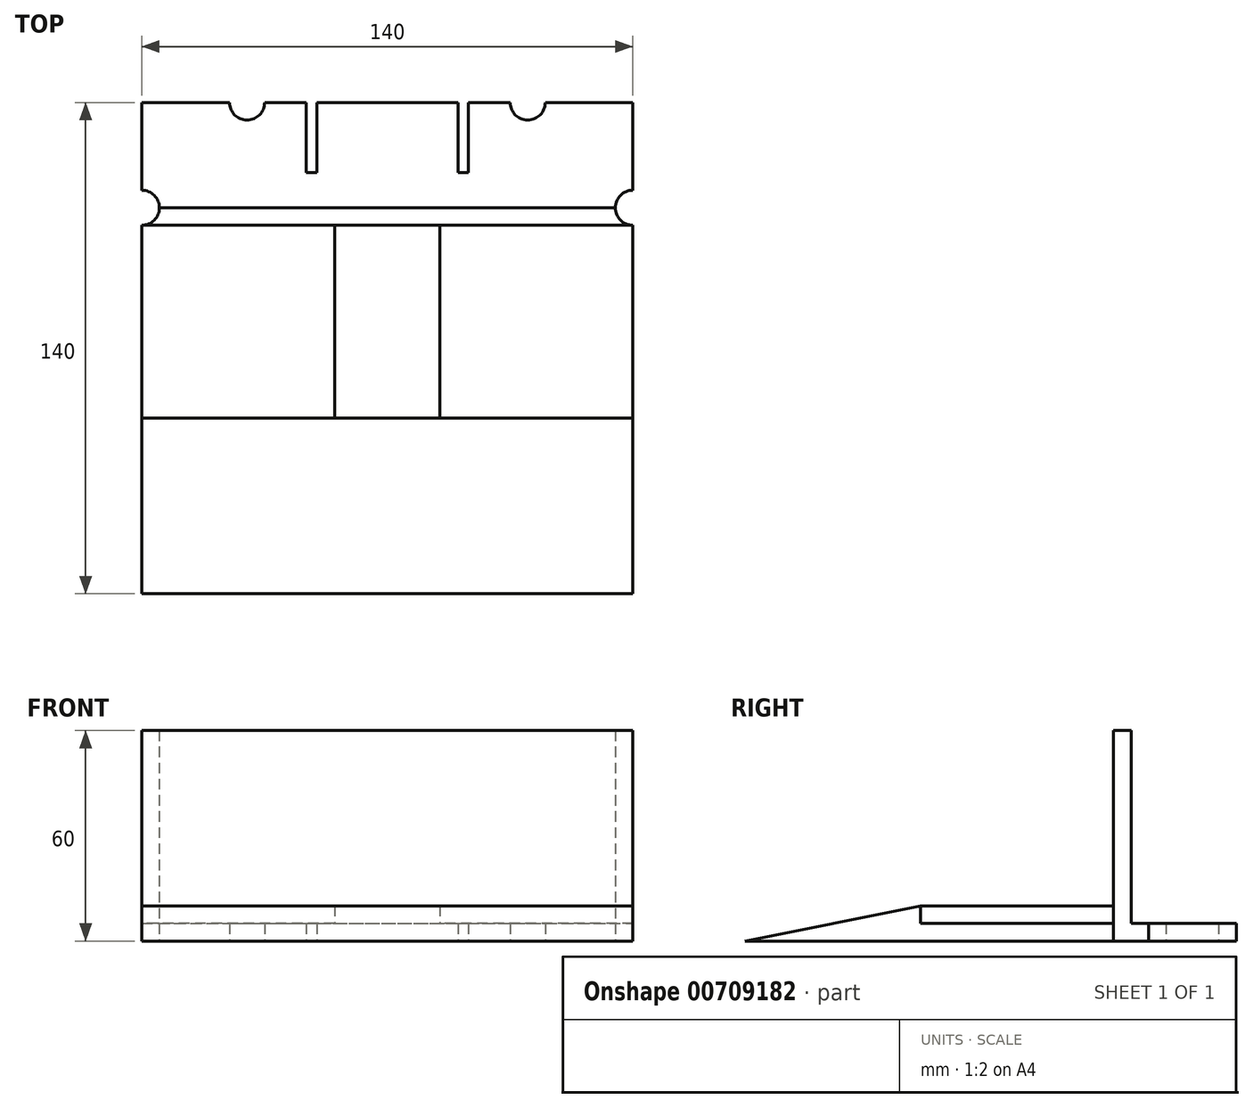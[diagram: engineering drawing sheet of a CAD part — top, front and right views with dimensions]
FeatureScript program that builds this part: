
annotation { "Feature Type Name" : "Feature", "Feature Type Description" : "" }
export const myFeature = defineFeature(function(context is Context, id is Id, definition is map)
    precondition{}
    {
        {
            var Q0;
            Q0=qCreatedBy(makeId("Top.planeOp"),FACE);
            var sketch = newSketch(context, id + "F0", { "sketchPlane" : qUnion([Q0])});
            skLineSegment(sketch, "E0.bottom", {"start": v(-70.6, 56.15) * mm, "end": v(-45.6, 56.15) * mm});
            skLineSegment(sketch, "E0.top", {"start": v(-70.6, -83.85) * mm, "end": v(69.4, -83.85) * mm});
            skLineSegment(sketch, "E0.left", {"start": v(-70.6, 56.15) * mm, "end": v(-70.6, 31.15) * mm});
            skLineSegment(sketch, "E0.right", {"start": v(69.4, 56.15) * mm, "end": v(69.4, 31.15) * mm});
            skLineSegment(sketch, "E1.top", {"start": v(-65.6, 26.15) * mm, "end": v(-40.6, 26.15) * mm});
            skLineSegment(sketch, "E1.right", {"start": v(-40.6, 51.15) * mm, "end": v(-40.6, 26.15) * mm});
            skArc(sketch, "E2", {"start": v(-70.6, 21.15) * mm, "mid": v(-65.6, 26.15) * mm, "end": v(-70.6, 31.15) * mm});
            skArc(sketch, "E3", {"start": v(-45.6, 56.15) * mm, "mid": v(-40.6, 51.15) * mm, "end": v(-35.6, 56.15) * mm});
            skLineSegment(sketch, "E4.trimOffspring", {"start": v(-70.6, 21.15) * mm, "end": v(-70.6, -83.85) * mm});
            skLineSegment(sketch, "E5.trimOffspring", {"start": v(-35.6, 56.15) * mm, "end": v(-23.71, 56.15) * mm});
            skArc(sketch, "E6.MirrorCS", {"start": v(44.4, 56.15) * mm, "mid": v(39.4, 51.15) * mm, "end": v(34.4, 56.15) * mm});
            skLineSegment(sketch, "E7.MirrorCS", {"start": v(64.4, 26.15) * mm, "end": v(39.4, 26.15) * mm});
            skLineSegment(sketch, "E8.MirrorCS", {"start": v(39.4, 51.15) * mm, "end": v(39.4, 26.15) * mm});
            skArc(sketch, "E9.MirrorCS", {"start": v(69.4, 21.15) * mm, "mid": v(64.4, 26.15) * mm, "end": v(69.4, 31.15) * mm});
            skLineSegment(sketch, "E10.trimOffspring", {"start": v(44.4, 56.15) * mm, "end": v(69.4, 56.15) * mm});
            skLineSegment(sketch, "E11.trimOffspring", {"start": v(69.4, 21.15) * mm, "end": v(69.4, -83.85) * mm});
            skLineSegment(sketch, "E12", {"start": v(-23.71, 36.15) * mm, "end": v(-20.71, 36.15) * mm});
            skLineSegment(sketch, "E13.top", {"start": v(-20.71, 36.15) * mm, "end": v(-23.71, 36.15) * mm});
            skLineSegment(sketch, "E13.left", {"start": v(-20.71, 56.15) * mm, "end": v(-20.71, 36.15) * mm});
            skLineSegment(sketch, "E13.right", {"start": v(-23.71, 56.15) * mm, "end": v(-23.71, 36.15) * mm});
            skLineSegment(sketch, "E14.MirrorCS", {"start": v(22.53, 56.15) * mm, "end": v(22.53, 36.15) * mm});
            skLineSegment(sketch, "E15.MirrorCS", {"start": v(19.53, 56.15) * mm, "end": v(19.53, 36.15) * mm});
            skLineSegment(sketch, "E16.trimOffspring", {"start": v(19.53, 36.15) * mm, "end": v(22.53, 36.15) * mm});
            skLineSegment(sketch, "E17.trimOffspring", {"start": v(22.53, 56.15) * mm, "end": v(34.4, 56.15) * mm});
            skLineSegment(sketch, "E18.trimOffspring", {"start": v(-20.71, 56.15) * mm, "end": v(19.53, 56.15) * mm});
            skLineSegment(sketch, "E19", {"start": v(-70.6, -33.85) * mm, "end": v(69.4, -33.85) * mm});
            skLineSegment(sketch, "E20", {"start": v(-70.6, 26.15) * mm, "end": v(69.4, 26.15) * mm});
            skLineSegment(sketch, "E21", {"start": v(-20.71, 36.15) * mm, "end": v(19.53, 36.15) * mm});
            skLineSegment(sketch, "E22", {"start": v(-70.6, 21.15) * mm, "end": v(69.4, 21.15) * mm});
            skLineSegment(sketch, "E23.trimOffspring", {"start": v(-15.6, 21.15) * mm, "end": v(-15.6, -33.85) * mm});
            skLineSegment(sketch, "E24.trimOffspring", {"start": v(14.4, 21.15) * mm, "end": v(14.4, -33.85) * mm});
            skSolve(sketch);
        }
        {
            var Q0;
            {var subQ0=sQuery(id+"F0.wireOp",EDGE,"E20");var subQ1=sQuery(id+"F0.wireOp",EDGE,"AWKKnLec-caKo-ObTL-4XCA-oNwnjQ9TKeaN");var subQ2=makeQuery(id+"F0.imprint","INTERSECT",VERTEX,{"derivedFrom":[subQ1,subQ0]});Q0=makeQuery(id+"F0.imprint","IMPRINT",FACE,{"disambiguationData":[TD([[makeQuery(id+"F0.imprint","IMPRINT",EDGE,{"disambiguationData":[TD([[subQ2,-1.0]])],"derivedFrom":subQ1}),1.0]])]});}
            var Q1;
            {var subQ0=sQuery(id+"F0.wireOp",EDGE,"E20");var subQ1=sQuery(id+"F0.wireOp",EDGE,"AWKKnLec-caKo-ObTL-4XCA-oNwnjQ9TKeaN");var subQ2=makeQuery(id+"F0.imprint","INTERSECT",VERTEX,{"derivedFrom":[subQ1,subQ0]});Q1=makeQuery(id+"F0.imprint","IMPRINT",FACE,{"disambiguationData":[TD([[makeQuery(id+"F0.imprint","IMPRINT",EDGE,{"disambiguationData":[TD([[subQ2,-1.0]])],"derivedFrom":subQ1}),-1.0]])]});}
            var Q2;
            {var subQ0=sQuery(id+"F0.wireOp",EDGE,"E1.top");Q2=makeQuery(id+"F0.imprint","IMPRINT",FACE,{"disambiguationData":[TD([[makeQuery(id+"F0.imprint","IMPRINT",EDGE,{"derivedFrom":subQ0}),-1.0]])]});}
            var Q3;
            {var subQ3=sQuery(id+"F0.wireOp",EDGE,"E0.bottom");Q3=makeQuery(id+"F0.imprint","IMPRINT",FACE,{"disambiguationData":[TD([[makeQuery(id+"F0.imprint","IMPRINT",EDGE,{"derivedFrom":subQ3}),-1.0]])]});}
            var Q4;
            Q4=makeQuery(id+"F0.imprint","IMPRINT",FACE,{"disambiguationData":[TD([[makeQuery(id+"F0.imprint","IMPRINT",EDGE,{"derivedFrom":sQuery(id+"F0.wireOp",EDGE,"E13.left")}),1.0]])]});
            var Q5;
            Q5=makeQuery(id+"F0.imprint","IMPRINT",FACE,{"disambiguationData":[TD([[makeQuery(id+"F0.imprint","IMPRINT",EDGE,{"derivedFrom":sQuery(id+"F0.wireOp",EDGE,"E13.left")}),1.0]])]});
            var Q6;
            {var subQ8=sQuery(id+"F0.wireOp",EDGE,"E7.MirrorCS");Q6=makeQuery(id+"F0.imprint","IMPRINT",FACE,{"disambiguationData":[TD([[makeQuery(id+"F0.imprint","IMPRINT",EDGE,{"derivedFrom":subQ8}),1.0]])]});}
            var Q7;
            {var subQ4=sQuery(id+"F0.wireOp",EDGE,"E0.right");Q7=makeQuery(id+"F0.imprint","IMPRINT",FACE,{"disambiguationData":[TD([[makeQuery(id+"F0.imprint","IMPRINT",EDGE,{"derivedFrom":subQ4}),-1.0]])]});}
            var Q8;
            {var subQ1=sQuery(id+"F0.wireOp",EDGE,"E1.right");Q8=makeQuery(id+"F0.imprint","IMPRINT",FACE,{"disambiguationData":[TD([[makeQuery(id+"F0.imprint","IMPRINT",EDGE,{"derivedFrom":subQ1}),1.0]])]});}
            var Q9;
            {var subQ1=sQuery(id+"F0.wireOp",EDGE,"E1.top");Q9=makeQuery(id+"F0.imprint","IMPRINT",FACE,{"disambiguationData":[TD([[makeQuery(id+"F0.imprint","IMPRINT",EDGE,{"derivedFrom":subQ1}),-1.0]])]});}
            var Q10;
            {var subQ5=sQuery(id+"F0.wireOp",EDGE,"E23.trimOffspring");Q10=makeQuery(id+"F0.imprint","IMPRINT",FACE,{"disambiguationData":[TD([[makeQuery(id+"F0.imprint","IMPRINT",EDGE,{"derivedFrom":subQ5}),-1.0]])]});}
            var Q11;
            {var subQ5=sQuery(id+"F0.wireOp",EDGE,"E24.trimOffspring");Q11=makeQuery(id+"F0.imprint","IMPRINT",FACE,{"disambiguationData":[TD([[makeQuery(id+"F0.imprint","IMPRINT",EDGE,{"derivedFrom":subQ5}),1.0]])]});}
            extrude(context, id + "F1", {"entities" : qUnion([Q0, Q1, Q2, Q3, Q4, Q5, Q6, Q7, Q8, Q9, Q10, Q11]), "depth" : 5 * mm, "offsetDistance" : 25 * mm});
        }
        {
            var Q0;
            {var subQ2=sQuery(id+"F0.wireOp",EDGE,"E23.trimOffspring");Q0=makeQuery(id+"F0.imprint","IMPRINT",FACE,{"disambiguationData":[TD([[makeQuery(id+"F0.imprint","IMPRINT",EDGE,{"derivedFrom":subQ2}),1.0]])]});}
            var Q1;
            {var subQ5=sQuery(id+"F0.wireOp",EDGE,"E0.top");Q1=makeQuery(id+"F0.imprint","IMPRINT",FACE,{"disambiguationData":[TD([[makeQuery(id+"F0.imprint","IMPRINT",EDGE,{"derivedFrom":subQ5}),1.0]])]});}
            extrude(context, id + "F2", {"entities" : qUnion([Q0, Q1]), "operationType" : NewBodyOperationType.ADD, "depth" : 10 * mm, "offsetDistance" : 25 * mm});
        }
        {
            var Q0;
            {var subQ0=sQuery(id+"F0.wireOp",EDGE,"E4.trimOffspring");Q0=makeQuery(id+"F2.boolean.opBoolean","MERGE",FACE,{"derivedFrom":[makeQuery(id+"F1.opExtrude","SWEPT_FACE",FACE,{"disambiguationData":[OSD([subQ0])]}),makeQuery(id+"F2.opExtrude","SWEPT_FACE",FACE,{"disambiguationData":[OSD([subQ0])]})]});}
            var sketch = newSketch(context, id + "F3", { "sketchPlane" : qUnion([Q0])});
            skLineSegment(sketch, "E25", {"start": v(33.85, 10) * mm, "end": v(83.85, 0) * mm});
            skSolve(sketch);
        }
        {
            var Q0;
            Q0=makeQuery(id+"F3.imprint","IMPRINT",FACE,{"disambiguationData":[TD([[makeQuery(id+"F3.imprint","IMPRINT",EDGE,{"derivedFrom":sQuery(id+"F3.wireOp",EDGE,"E25")}),1.0]])]});
            extrude(context, id + "F4", {"entities" : qUnion([Q0]), "operationType" : NewBodyOperationType.REMOVE, "oppositeDirection" : true, "depth" : 141 * mm, "offsetDistance" : 25 * mm});
        }
        {
            var Q0;
            {var subQ1=sQuery(id+"F0.wireOp",EDGE,"E1.top");Q0=makeQuery(id+"F0.imprint","IMPRINT",FACE,{"disambiguationData":[TD([[makeQuery(id+"F0.imprint","IMPRINT",EDGE,{"derivedFrom":subQ1}),-1.0]])]});}
            extrude(context, id + "F5", {"entities" : qUnion([Q0]), "operationType" : NewBodyOperationType.ADD, "depth" : 60 * mm, "offsetDistance" : 25 * mm});
        }
    });
